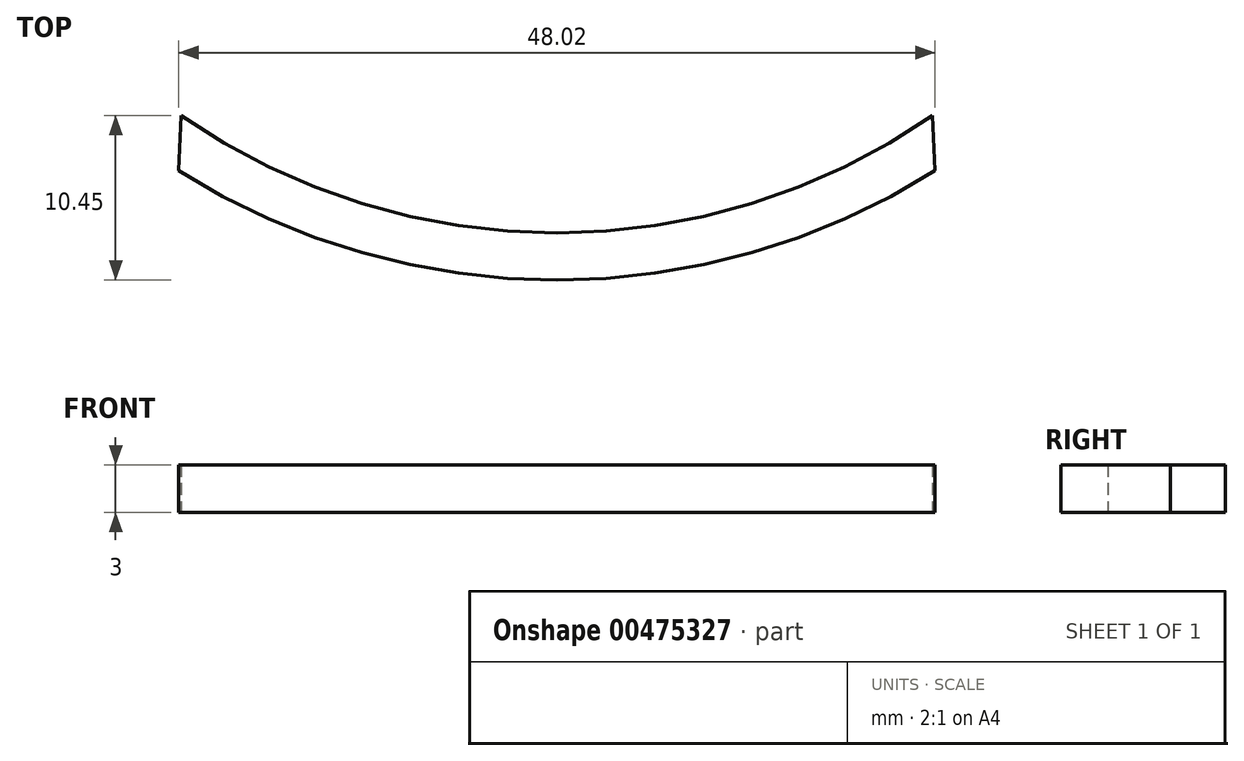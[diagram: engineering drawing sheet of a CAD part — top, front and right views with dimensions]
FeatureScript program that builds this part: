
annotation { "Feature Type Name" : "Feature", "Feature Type Description" : "" }
export const myFeature = defineFeature(function(context is Context, id is Id, definition is map)
    precondition{}
    {
        {
            var Q0;
            Q0=qCreatedBy(makeId("Top.planeOp"),FACE);
            var sketch = newSketch(context, id + "F0", { "sketchPlane" : qUnion([Q0])});
            skArc(sketch, "E0", {"start": v(0, 0) * mm, "mid": v(12.5, 1.77) * mm, "end": v(24.01, 6.95) * mm});
            skArc(sketch, "E1", {"start": v(0, 0) * mm, "mid": v(-12.5, 1.77) * mm, "end": v(-24.01, 6.95) * mm});
            skArc(sketch, "E2", {"start": v(0, 3) * mm, "mid": v(-12.5, 4.9) * mm, "end": v(-23.87, 10.45) * mm});
            skArc(sketch, "E3", {"start": v(0, 3) * mm, "mid": v(12.5, 4.9) * mm, "end": v(23.87, 10.45) * mm});
            skLineSegment(sketch, "E4", {"start": v(23.87, 10.45) * mm, "end": v(24.01, 6.95) * mm});
            skLineSegment(sketch, "E5", {"start": v(-23.87, 10.45) * mm, "end": v(-24.01, 6.95) * mm});
            skPoint(sketch, "E6.start.orphan", {"position": v(0, 1.96) * mm});
            skSolve(sketch);
        }
        {
            var Q0;
            Q0=makeQuery(id+"F0.imprint","IMPRINT",FACE,{"disambiguationData":[TD([[makeQuery(id+"F0.imprint","IMPRINT",EDGE,{"derivedFrom":sQuery(id+"F0.wireOp",EDGE,"E0")}),1.0]])]});
            extrude(context, id + "F1", {"entities" : qUnion([Q0]), "depth" : 3 * mm});
        }
    });
